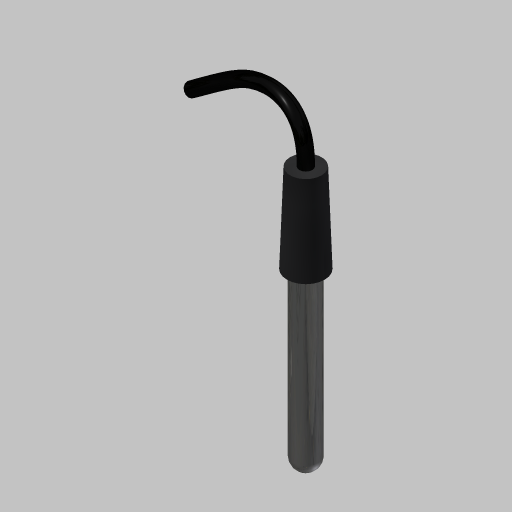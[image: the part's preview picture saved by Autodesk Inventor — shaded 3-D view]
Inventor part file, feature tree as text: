
AUTODESK INVENTOR PART (.ipt)
format: ipt  version: 2023 (Build 270158000, 158)  size: 164,352 bytes
history: native  units: mm
features: sketch x4, extrude x2, fillet x1, sweep x1, projected_geometry x1
ambient origin geometry x8: Origin, YZ Plane, XZ Plane, XY Plane, X Axis, Y Axis, Z Axis, Center Point
bodies: Solid1 (feature_tree)
feature tree (9):
  extrude  "Extrusion1"  Depth=30.8mm TaperAngle=0.0deg
  fillet  "Fillet1"  Radius=1.5mm
  sweep  "Sweep1"
  extrude  "Extrusion2"  Depth=10.4mm
  sketch  "Sketch1"  dims[d0=3.0mm d1=30.8mm d2=0.0mm d3=1.5mm]
  sketch  "Sketch2"  dims[d4=0.0mm d5=0.0mm d6=2.0mm d7=0.0mm]
  sketch  "Sketch3"  dims[d8=3.7mm d9=10.4mm d10=0.349066mm]
  sketch  "Sketch4"  dims[d11=6.0mm]
  projected_geometry  "Projected Loop1"
